# Revit family: IS_Strada_A6852_BIM_DE
name_source: partatom
category: Plumbing Fixtures
revit_build: Autodesk Revit MEP 2016 (Build: 20161004_0715(x64)
units: mm (PartAtom-declared; Revit-internal decimal feet)

## family parameters
Always vertical = No
Cut with Voids When Loaded = No
OmniClass Number = 23.45.55.17
OmniClass Title = Mixing Faucets
Part Type = Normal
Room Calculation Point = No
Round Connector Dimension = Use Diameter
Shared = No
Work Plane-Based = No

## types (1)
- A6852AA - STRADA build-in shower single lever mixer
    Accessories = www.idealstandard.de\ersatzteile
    AreaUnits = millimeters
    AssetType = Fixed
    BIMObjectName = ISI_IdealStandard_
    BIMobject category = Taps & Mixers
    BOSUseNativeGeometries = 1
    BarCode = 4015413332361
    Brand = Ideal Standard
    Brand url = http://www.idealstandard.co.uk
    CodePerformance = 0
    Color = Chrome
    ConnectionType = Plumbing
    Cost = 0 $
    CurrencyUnit = €
    CurrentRevision = 1
    Date of publishing = 43049
    Description = IS Brausearmatur UP STRADA, Bausatz 2, Rosette 157x157mm, Chrom
    DurationUnit = year
    EAN code = https://4015413332361
    Edition number = 1
    ExpectedLife = 25
    FaucetFunction = mixed
    FaucetOperation = leverhandle
    FaucetType = pillar
    Features = STRADA build-in shower single lever mixer
    Finish = Chrome
    IFC Classification = Sanitary Terminal
    IfcExportAs = Ifc Valve Type
    Installation instructions = http://www.idealstandard.de
    InstallationInstructions = www.idealstandard.de\produkte
    LinearUnits = millimeters
    MainColor = Chrome
    MaintenanceInformation = www.idealstandard.de\produkte
    Manufacturer name = Ideal Standard
    ManufacturerURL = http://www.idealstandard.com
    Material = Brass
    Material main = Brass
    Model = A6852AA
    ModelNumber = A6852AA
    ModelReference = IS Brausearmatur UP STRADA, Bausatz 2, Rosette 157x157mm, Chrom
    NettWeight = 1,636 kg
    Nominal height = 183
    Nominal width = 157
    NominalDepth = 87 mm  [stored 0.285433 ft]
    NominalHeight = 183 mm  [stored 0.600394 ft]
    NominalLength = 87 mm  [stored 0.285433 ft]
    NominalWidth = 157 mm  [stored 0.515092 ft]
    Product Guid = 0e6eba9f-8d19-4751-84f8-80bfab693cf3
    Product SKU = A6852
    Product data url = https://bimobject.com
    Product family = STRADA
    Product group = Shower Mixer
    Product name = STRADA build-in shower single lever mixer
    Product url = http://www.idealstandard.de
    ProductInformation = http://www.idealstandard.de
    QR code = http://bimobject.com
    Shape = Sculptured
    Size = 183 x 87 x 157mm
    Space = Internal
    SpareParts = www.idealstandard.de/ersatzteile
    Technical description = http://www.idealstandard.de
    TestPressure = 10 Bar
    URL = http://www.idealstandard.de
    Uniclass2015Version = Products v1.1
    ValveMechanism = ceramic disc
    ValveOperation = lever
    Version = 1
    VolumeUnits = Litres
    Weight Net (Kg) = 1.64
    WorkingPressure = 1-5 Bar

note: [stored X ft] marks values corroborated as IEEE doubles in the binary element streams (Revit-internal decimal feet)

## geometry (parser evidence)
native form markers: Blend x4, Sweep x1
no freeform markers — native parametric forms only
